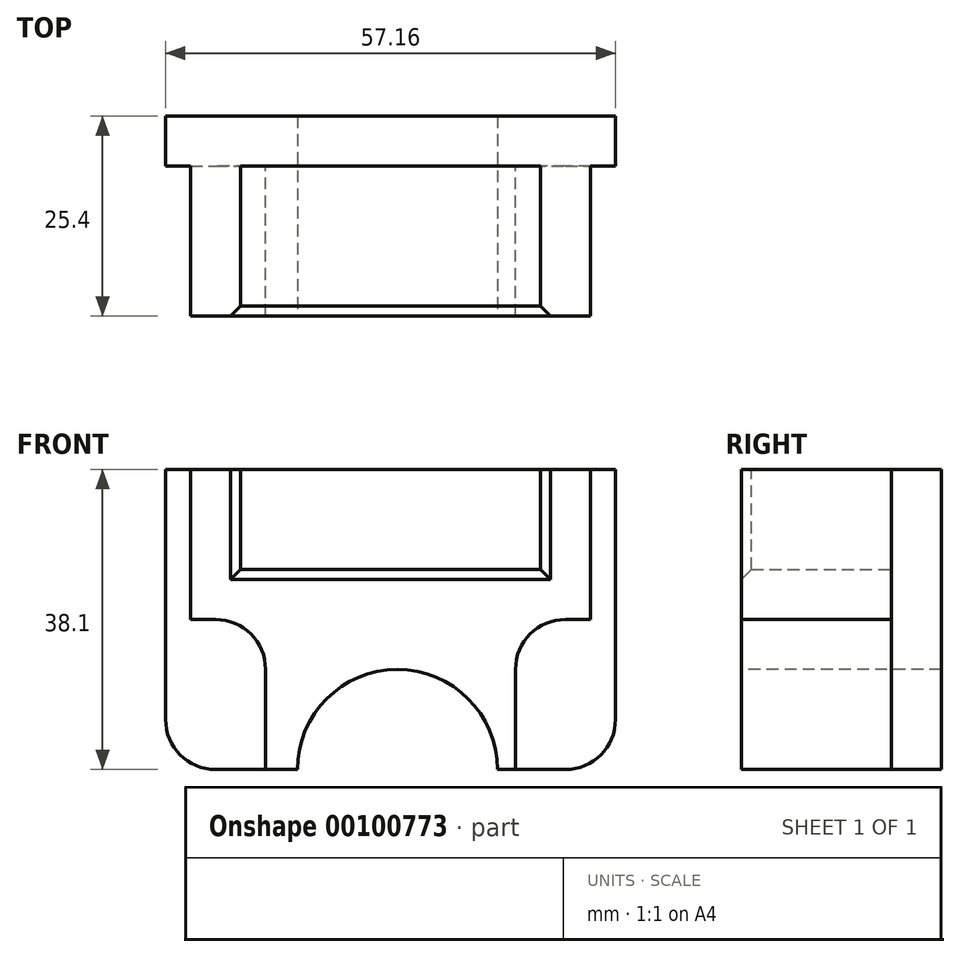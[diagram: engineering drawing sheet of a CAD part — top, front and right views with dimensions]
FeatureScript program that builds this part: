
annotation { "Feature Type Name" : "Feature", "Feature Type Description" : "" }
export const myFeature = defineFeature(function(context is Context, id is Id, definition is map)
    precondition{}
    {
        {
            var Q0;
            Q0=qCreatedBy(makeId("Front.planeOp"),FACE);
            var sketch = newSketch(context, id + "F0", { "sketchPlane" : qUnion([Q0])});
            skLineSegment(sketch, "E0.bottom", {"start": v(-28.57, 19.05) * mm, "end": v(28.58, 19.05) * mm});
            skLineSegment(sketch, "E0.top", {"start": v(-28.58, -19.05) * mm, "end": v(28.57, -19.05) * mm});
            skLineSegment(sketch, "E0.left", {"start": v(-28.58, 19.05) * mm, "end": v(-28.58, -19.05) * mm});
            skLineSegment(sketch, "E0.right", {"start": v(28.58, 19.05) * mm, "end": v(28.57, -19.05) * mm});
            skPoint(sketch, "E0.middle", {"position": v(0, 0) * mm});
            skSolve(sketch);
        }
        {
            var Q0;
            Q0 = qSketchRegion(id + "F0", true);
            extrude(context, id + "F1", {"entities" : qUnion([Q0]), "oppositeDirection" : true, "depth" : 6.35 * mm});
        }
        {
            var Q0;
            Q0=makeQuery(id+"F1.opExtrude","CAP_FACE",FACE,{"disambiguationData":[OSD([sQuery(id+"F0.wireOp",EDGE,"E0.bottom"),sQuery(id+"F0.wireOp",EDGE,"E0.top"),sQuery(id+"F0.wireOp",EDGE,"E0.left"),sQuery(id+"F0.wireOp",EDGE,"E0.right")])],"isStart":true});
            var sketch = newSketch(context, id + "F2", { "sketchPlane" : qUnion([Q0])});
            skLineSegment(sketch, "E1.bottom", {"start": v(-25.4, 19.05) * mm, "end": v(-19.05, 19.05) * mm});
            skLineSegment(sketch, "E1.top", {"start": v(-15.88, -19.05) * mm, "end": v(15.88, -19.05) * mm});
            skLineSegment(sketch, "E1.left", {"start": v(-25.4, 19.05) * mm, "end": v(-25.4, 0) * mm});
            skLineSegment(sketch, "E1.right", {"start": v(25.4, 19.05) * mm, "end": v(25.4, 0) * mm});
            skPoint(sketch, "E1.middle", {"position": v(0, 0) * mm});
            skLineSegment(sketch, "E2.top", {"start": v(19.05, 6.35) * mm, "end": v(-19.05, 6.35) * mm});
            skLineSegment(sketch, "E2.left", {"start": v(19.05, 19.05) * mm, "end": v(19.05, 6.35) * mm});
            skLineSegment(sketch, "E2.right", {"start": v(-19.05, 19.05) * mm, "end": v(-19.05, 6.35) * mm});
            skLineSegment(sketch, "E3.top", {"start": v(25.4, 0) * mm, "end": v(15.88, 0) * mm});
            skLineSegment(sketch, "E3.right", {"start": v(15.88, -19.05) * mm, "end": v(15.88, 0) * mm});
            skLineSegment(sketch, "E4", {"start": v(0, -22.43) * mm, "end": v(0, 24.78) * mm, "construction": true});
            skPoint(sketch, "E4.endSnap0", {"position": v(0, 19.05) * mm});
            skLineSegment(sketch, "E5.MirrorCS", {"start": v(-25.4, 0) * mm, "end": v(-15.87, 0) * mm});
            skLineSegment(sketch, "E6.MirrorCS", {"start": v(-15.88, -19.05) * mm, "end": v(-15.88, 0) * mm});
            skPoint(sketch, "E7.orphan", {"position": v(-25.4, -19.05) * mm});
            skPoint(sketch, "E3.bottom.start.orphan", {"position": v(25.4, -19.05) * mm});
            skLineSegment(sketch, "E8.trimOffspring", {"start": v(19.05, 19.05) * mm, "end": v(25.4, 19.05) * mm});
            skSolve(sketch);
        }
        {
            var Q0;
            Q0 = qSketchRegion(id + "F2", true);
            extrude(context, id + "F3", {"entities" : qUnion([Q0]), "operationType" : NewBodyOperationType.ADD, "depth" : 19.05 * mm});
        }
        {
            var Q0;
            Q0=makeQuery(id+"F3.opExtrude","CAP_FACE",FACE,{"disambiguationData":[OSD([sQuery(id+"F2.wireOp",EDGE,"E1.bottom"),sQuery(id+"F2.wireOp",EDGE,"E1.top"),sQuery(id+"F2.wireOp",EDGE,"E1.left"),sQuery(id+"F2.wireOp",EDGE,"E1.right"),sQuery(id+"F2.wireOp",EDGE,"E2.top"),sQuery(id+"F2.wireOp",EDGE,"E2.left"),sQuery(id+"F2.wireOp",EDGE,"E2.right"),sQuery(id+"F2.wireOp",EDGE,"E3.top"),sQuery(id+"F2.wireOp",EDGE,"E3.right"),sQuery(id+"F2.wireOp",EDGE,"E5.MirrorCS"),sQuery(id+"F2.wireOp",EDGE,"E6.MirrorCS"),sQuery(id+"F2.wireOp",EDGE,"E8.trimOffspring")])],"isStart":false});
            var sketch = newSketch(context, id + "F4", { "sketchPlane" : qUnion([Q0])});
            skArc(sketch, "E9", {"start": v(13.57, -19.05) * mm, "mid": v(0.87, -6.35) * mm, "end": v(-11.83, -19.05) * mm});
            skLineSegment(sketch, "E10", {"start": v(13.57, -19.05) * mm, "end": v(-11.83, -19.05) * mm});
            skSolve(sketch);
        }
        {
            var Q0;
            Q0 = qSketchRegion(id + "F4", true);
            extrude(context, id + "F5", {"entities" : qUnion([Q0]), "operationType" : NewBodyOperationType.REMOVE, "endBound" : BoundingType.THROUGH_ALL, "oppositeDirection" : true, "depth" : 25.4 * mm});
        }
        {
            var Q0;
            Q0=makeQuery(id+"F1.opExtrude","SWEPT_EDGE",EDGE,{"disambiguationData":[OSD([sQuery(id+"F0.wireOp",EDGE,"E0.top"),sQuery(id+"F0.wireOp",EDGE,"E0.left")])]});
            var Q1;
            Q1=makeQuery(id+"F1.opExtrude","SWEPT_EDGE",EDGE,{"disambiguationData":[OSD([sQuery(id+"F0.wireOp",EDGE,"E0.top"),sQuery(id+"F0.wireOp",EDGE,"E0.right")])]});
            var Q2;
            Q2=makeQuery(id+"F3.opExtrude","SWEPT_EDGE",EDGE,{"disambiguationData":[OSD([sQuery(id+"F2.wireOp",EDGE,"E3.top"),sQuery(id+"F2.wireOp",EDGE,"E3.right")])]});
            var Q3;
            Q3=makeQuery(id+"F3.opExtrude","SWEPT_EDGE",EDGE,{"disambiguationData":[OSD([sQuery(id+"F2.wireOp",EDGE,"E5.MirrorCS"),sQuery(id+"F2.wireOp",EDGE,"E6.MirrorCS")])]});
            fillet(context, id + "F6", {"entities" : qUnion([Q0, Q1, Q2, Q3]), "radius" : 6.35 * mm, "tangentPropagation" : true, "allowEdgeOverflow" : false});
        }
        {
            var Q0;
            Q0=makeQuery(id+"F5.boolean.opBoolean","COPY",EDGE,{"derivedFrom":makeQuery(id+"F5.opExtrude","CAP_EDGE",EDGE,{"disambiguationData":[OSD([sQuery(id+"F4.wireOp",EDGE,"E9")])],"isStart":true})});
            var Q1;
            Q1=makeQuery(id+"F3.opExtrude","CAP_EDGE",EDGE,{"disambiguationData":[OSD([sQuery(id+"F2.wireOp",EDGE,"E2.top")])],"isStart":false});
            var Q2;
            Q2=makeQuery(id+"F3.opExtrude","CAP_EDGE",EDGE,{"disambiguationData":[OSD([sQuery(id+"F2.wireOp",EDGE,"E2.right")])],"isStart":false});
            var Q3;
            Q3=makeQuery(id+"F3.opExtrude","CAP_EDGE",EDGE,{"disambiguationData":[OSD([sQuery(id+"F2.wireOp",EDGE,"E2.left")])],"isStart":false});
            chamfer(context, id + "F7", {"entities" : qUnion([Q0, Q1, Q2, Q3]), "width" : 1.27 * mm, "tangentPropagation" : true});
        }
    });
